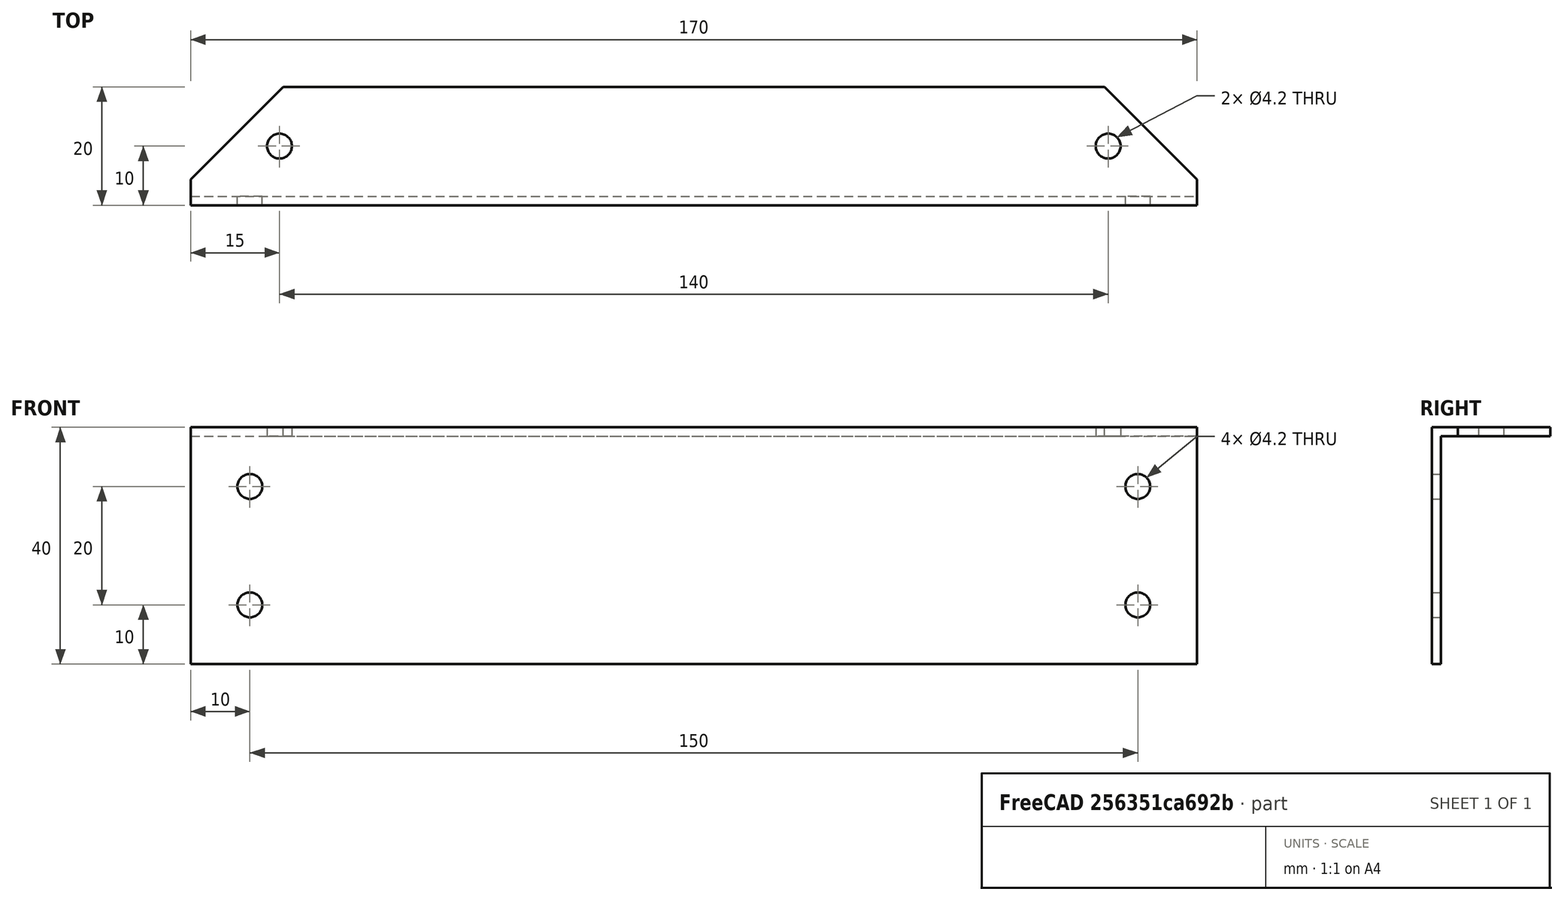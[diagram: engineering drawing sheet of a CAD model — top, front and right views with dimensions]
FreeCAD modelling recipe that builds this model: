
FCSTD DOCUMENT  (FreeCAD 1.0R39319 (Git))
Label: OCT-UBRAC-AA
License: All rights reserved
LicenseURL: https://en.wikipedia.org/wiki/All_rights_reserved
objects: TechDraw::DrawViewDimension×16, Sketcher::SketchObject×4, TechDraw::DrawProjGroupItem×3, PartDesign::Hole×2, PartDesign::Pad×1, PartDesign::Pocket×1, App::VarSet×1, PartDesign::Mirrored×1, PartDesign::Body×1, TechDraw::DrawSVGTemplate×1, TechDraw::DrawProjGroup×1, TechDraw::DrawPage×1
note: 50 computed .brp shape members not serialized (recipe doc carries the construction recipe); baked Part::Feature solids carry a one-line shape summary decoded from their .brp

FEATURE [Sketcher::SketchObject] Sketch
  ArcFitTolerance = 1e-06
  AttachmentSupport = -> [YZ_Plane]
  FullyConstrained = true
  MakeInternals = false
  MapMode = 5
  Placement = pos=(0,0,0) rot=(0.57735,0.57735,0.57735;2.0944rad)
  sketch-geometry (6):
    g0: LineSegment StartX=0 StartY=-40 StartZ=0 EndX=0 EndY=0 EndZ=0
    g1: LineSegment StartX=0 StartY=0 StartZ=0 EndX=20 EndY=0 EndZ=0
    g2: LineSegment StartX=20 StartY=0 StartZ=0 EndX=20 EndY=-1.5 EndZ=0
    g3: LineSegment StartX=20 StartY=-1.5 StartZ=0 EndX=1.5 EndY=-1.5 EndZ=0
    g4: LineSegment StartX=1.5 StartY=-1.5 StartZ=0 EndX=1.5 EndY=-40 EndZ=0
    g5: LineSegment StartX=1.5 StartY=-40 StartZ=0 EndX=0 EndY=-40 EndZ=0
  constraints (17):
    c: Coincident(g0,g1)
    c: Horizontal(g1)
    c: Coincident(g1,g2)
    c: Coincident(g2,g3)
    c: Coincident(g3,g4)
    c: Coincident(g4,g5)
    c: Coincident(g5,g0)
    c: Coincident(g0,g-1)
    c: Vertical(g2)
    c: Horizontal(g5)
    c: Vertical(g0)
    c: Vertical(g4)
    c: Horizontal(g3)
    c: DistanceX(g5,g5) = 1.5
    c: DistanceY(g0,g0) = 40
    c: DistanceY(g2,g2) = 1.5
    c: DistanceX(g1,g1) = 20
FEATURE [PartDesign::Pad] Pad
  Direction = (1,0,0)
  Length = 170
  Length2 = 10
  Midplane = true
  Placement = pos=(0,0,0) rot=(1,1,1;2.0944rad)
  Profile = -> Sketch
  ReferenceAxis = -> Sketch [N_Axis]
  Refine = true
  Suppressed = false
  Type = 0
FEATURE [Sketcher::SketchObject] Sketch002
  ArcFitTolerance = 1e-06
  AttachmentSupport = -> [XZ_Plane]
  FullyConstrained = true
  MakeInternals = false
  MapMode = 5
  Placement = pos=(0,0,0) rot=(1,0,0;1.5708rad)
  sketch-geometry (5):
    g0: Circle CenterX=-75 CenterY=-30 CenterZ=0 NormalX=0 NormalY=0 NormalZ=1 AngleXU=0 Radius=2.5
    g1: Circle CenterX=75 CenterY=-30 CenterZ=0 NormalX=0 NormalY=0 NormalZ=1 AngleXU=0 Radius=2.5
    g2: Circle CenterX=-75 CenterY=-10 CenterZ=0 NormalX=0 NormalY=0 NormalZ=1 AngleXU=0 Radius=2.5
    g3: Circle CenterX=75 CenterY=-10 CenterZ=0 NormalX=0 NormalY=0 NormalZ=1 AngleXU=0 Radius=2.5
    g4: LineSegment [constr] StartX=-75 StartY=-30 StartZ=0 EndX=-75 EndY=-10 EndZ=0
  constraints (12):
    c: Symmetric(g0,g1,g-2)
    c: DistanceX(g0,g1) = 150
    c: Diameter(g0) = 5
    c: Equal(g1,g0)
    c: Symmetric(g3,g2,g-2)
    c: Coincident(g4,g0)
    c: Coincident(g4,g2)
    c: Vertical(g4)
    c: Equal(g2,g0)
    c: Equal(g0,g3)
    c: DistanceY(g4,g4) = 20
    c: DistanceY(g2,g-1) = 10
FEATURE [PartDesign::Hole] Hole  label="panel holes"
  BaseFeature = -> Pad
  CustomThreadClearance = 0
  Depth = 355.084
  DepthType = 1
  Diameter = 4.2
  DrillForDepth = false
  DrillPoint = 1
  DrillPointAngle = 118
  HoleCutCountersinkAngle = 90
  HoleCutCustomValues = false
  HoleCutDepth = 0
  HoleCutDiameter = 6.1
  HoleCutType = 0
  ModelThread = false
  Placement = pos=(0,0,0) rot=(1,1,1;2.0944rad)
  Profile = -> Sketch002
  Refine = true
  Suppressed = false
  Tapered = false
  TaperedAngle = 90
  ThreadClass = 0
  ThreadDepth = 355.084
  ThreadDepthType = 0
  ThreadDirection = 0
  ThreadFit = 0
  ThreadSize = 0
  ThreadType = 0
  Threaded = false
  UseCustomThreadClearance = false
FEATURE [Sketcher::SketchObject] Sketch003
  ArcFitTolerance = 1e-06
  AttachmentSupport = -> [XY_Plane]
  FullyConstrained = true
  MakeInternals = false
  MapMode = 5
  sketch-geometry (2):
    g0: Circle CenterX=-70 CenterY=10 CenterZ=0 NormalX=0 NormalY=0 NormalZ=1 AngleXU=0 Radius=2.5
    g1: Circle CenterX=70 CenterY=10 CenterZ=0 NormalX=0 NormalY=0 NormalZ=1 AngleXU=0 Radius=2.5
  constraints (5):
    c: Symmetric(g1,g0,g-2)
    c: DistanceX(g0,g1) = 140
    c: Equal(g0,g1)
    c: Diameter(g1) = 5
    c: Distance(g1,g-1) = 10
FEATURE [PartDesign::Hole] Hole001  label="base holes"
  BaseFeature = -> Hole
  CustomThreadClearance = 0
  Depth = 355.084
  DepthType = 1
  Diameter = 4.2
  DrillForDepth = false
  DrillPoint = 1
  DrillPointAngle = 118
  HoleCutCountersinkAngle = 90
  HoleCutCustomValues = false
  HoleCutDepth = 0
  HoleCutDiameter = 6.1
  HoleCutType = 0
  ModelThread = false
  Placement = pos=(0,0,0) rot=(1,1,1;2.0944rad)
  Profile = -> Sketch003
  Refine = true
  Suppressed = false
  Tapered = false
  TaperedAngle = 90
  ThreadClass = 0
  ThreadDepth = 355.084
  ThreadDepthType = 0
  ThreadDirection = 0
  ThreadFit = 0
  ThreadSize = 0
  ThreadType = 0
  Threaded = false
  UseCustomThreadClearance = false
FEATURE [Sketcher::SketchObject] Sketch004
  ArcFitTolerance = 1e-06
  AttachmentSupport = -> [XY_Plane]
  FullyConstrained = false
  MakeInternals = false
  MapMode = 5
  expr: Constraints[25] = <<dims>>.octWidth
  expr: Constraints[46] = <<dims>>.width / 2
  sketch-geometry (18):
    g0: LineSegment [constr] StartX=211 StartY=298.399 StartZ=0 EndX=87.3991 EndY=422 EndZ=0
    g1: LineSegment [constr] StartX=87.3991 StartY=422 StartZ=0 EndX=-87.3991 EndY=422 EndZ=0
    g2: LineSegment [constr] StartX=-87.3991 StartY=422 StartZ=0 EndX=-211 EndY=298.399 EndZ=0
    g3: LineSegment [constr] StartX=-211 StartY=298.399 StartZ=0 EndX=-211 EndY=123.601 EndZ=0
    g4: LineSegment [constr] StartX=-211 StartY=123.601 StartZ=0 EndX=-87.3991 EndY=0 EndZ=0
    g5: LineSegment [constr] StartX=-87.3991 StartY=0 StartZ=0 EndX=87.3991 EndY=0 EndZ=0
    g6: LineSegment [constr] StartX=87.3991 StartY=0 StartZ=0 EndX=211 EndY=123.601 EndZ=0
    g7: LineSegment [constr] StartX=211 StartY=123.601 StartZ=0 EndX=211 EndY=298.399 EndZ=0
    g8: Circle [constr] CenterX=0 CenterY=211 CenterZ=0 NormalX=0 NormalY=0 NormalZ=1 AngleXU=0 Radius=228.385
    g9: LineSegment [constr] StartX=-85 StartY=0 StartZ=0 EndX=-85 EndY=4.37763 EndZ=0
    g10: LineSegment StartX=-85 StartY=4.37763 StartZ=0 EndX=-85 EndY=50 EndZ=0
    g11: LineSegment StartX=-85 StartY=50 StartZ=0 EndX=-39.3776 EndY=50 EndZ=0
    g12: LineSegment StartX=-39.3776 StartY=50 StartZ=0 EndX=-85 EndY=4.37763 EndZ=0
    g13: LineSegment [constr] StartX=-89.0955 StartY=1.69639 StartZ=0 EndX=-76.7258 EndY=14.0661 EndZ=0
    g14: LineSegment [constr] StartX=-209.304 StartY=121.905 StartZ=0 EndX=-196.934 EndY=134.274 EndZ=0
    g15: LineSegment [constr] StartX=-196.934 StartY=134.274 StartZ=0 EndX=-76.7258 EndY=14.0661 EndZ=0
    g16: LineSegment [constr] StartX=-149.2 StartY=61.8005 StartZ=0 EndX=0 EndY=211 EndZ=0
    g17: LineSegment [constr] StartX=-85 StartY=4.37763 StartZ=0 EndX=-85.7071 EndY=5.08474 EndZ=0
  constraints (46):
    c: Coincident(g0,g1)
    c: Coincident(g1,g2)
    c: Coincident(g2,g3)
    c: Coincident(g3,g4)
    c: Coincident(g4,g5)
    c: Coincident(g5,g6)
    c: Coincident(g6,g7)
    c: Coincident(g7,g0)
    c: Equal(g0, g1-g7) x7
    c: PointOnObject(g0,g8)
    c: PointOnObject(g1,g8)
    c: PointOnObject(g2,g8)
    c: PointOnObject(g3,g8)
    c: PointOnObject(g4,g8)
    c: PointOnObject(g5,g8)
    c: PointOnObject(g6,g8)
    c: PointOnObject(g7,g8)
    c: PointOnObject(g8,g-2)
    c: Horizontal(g5)
    c: DistanceY(g5,g0) = 422
    c: PointOnObject(g5,g-1)
    c: PointOnObject(g9,g5)
    c: Vertical(g9)
    c: Coincident(g9,g10)
    c: Coincident(g10,g11)
    c: Horizontal(g11)
    c: Coincident(g11,g12)
    c: Coincident(g12,g10)
    c: Vertical(g10)
    c: Angle(g11,g12) = 0.785398
    c: PointOnObject(g13,g4)
    c: Coincident(g15,g14)
    c: Coincident(g15,g13)
    c: Perpendicular(g15,g13)
    c: Perpendicular(g15,g14)
    c: Perpendicular(g4,g14)
    c: Symmetric(g4,g4,g16)
    c: Coincident(g16,g8)
    c: Symmetric(g13,g14,g16)
    c: Distance(g15,g15) = 170
    c: DistanceX(g9,g-1) = 85
    c: Coincident(g17,g9)
    c: PointOnObject(g17,g13)
    c: Perpendicular(g13,g17)
    c: Distance(g17,g17) = 1
    c: DistanceY(g-1,g10) = 50
FEATURE [PartDesign::Pocket] Pocket
  BaseFeature = -> Hole001
  Direction = (0,0,-1)
  Length = 5
  Length2 = 5
  Placement = pos=(0,0,0) rot=(1,1,1;2.0944rad)
  Profile = -> Sketch004
  ReferenceAxis = -> Sketch004 [N_Axis]
  Refine = true
  Suppressed = false
  Type = 1
FEATURE [App::VarSet] VarSet  label="dims"
  octWidth = 422
  width = 170
FEATURE [PartDesign::Mirrored] Mirrored
  BaseFeature = -> Pocket
  MirrorPlane = -> YZ_Plane
  Originals = -> [Pocket]
  Placement = pos=(0,0,0) rot=(1,1,1;2.0944rad)
  Suppressed = false
  TransformMode = 0
FEATURE [PartDesign::Body] Body  label="OCT-UBRAC-AA"
  AllowCompound = false
  Group = -> [Sketch,Pad,Sketch002,Hole,Sketch003,Hole001,Sketch004,Pocket,Mirrored]
  Origin = -> Origin
  Tip = -> Mirrored
FEATURE [TechDraw::DrawSVGTemplate] Template
  EditableTexts = approval_person=S. Aphelion; creator=M. Stoll; date_of_issue=07/02/2026; document_status=Released; document_type=Component Drawing; drawing_number=DN; general_tolerances=+- 0.1 mm; language_code=EN; part_material=Aluminium; responsible_department=RD; revision_index=A; scale=1 : 1; sheet_number=1 / 1; supplementary_title_1=Frame Upper Bracket; title=OCT-UBRAC-AA
  Height = 297
  Orientation = 1
  Template = C:/Program Files/FreeCAD 1.0/data/Mod/TechDraw/Templates/A3_Landscape_ISO5457_advanced.svg
  Width = 420
FEATURE [TechDraw::DrawProjGroupItem] View  label="Front"
  CoarseView = false
  Direction = (0,-1,0)
  Focus = 100
  HardHidden = false
  IsoCount = 0
  IsoHidden = false
  IsoVisible = false
  LockPosition = true
  Perspective = false
  Rotation = 0
  RotationVector = (1,0,0)
  ScaleType = 2
  ScrubCount = 1
  SeamHidden = false
  SeamVisible = false
  SmoothHidden = false
  SmoothVisible = true
  Source = -> [Body]
  Type = 0
  X = 0
  XDirection = (1,0,0)
  Y = 0
FEATURE [TechDraw::DrawProjGroupItem] ProjItem  label="Right"
  CoarseView = false
  Direction = (1,-1e-16,0)
  Focus = 100
  HardHidden = false
  IsoCount = 0
  IsoHidden = false
  IsoVisible = false
  LockPosition = false
  Perspective = false
  Rotation = 0
  RotationVector = (1,0,0)
  ScaleType = 0
  ScrubCount = 1
  SeamHidden = false
  SeamVisible = false
  SmoothHidden = false
  SmoothVisible = true
  Source = -> [Body]
  Type = 2
  X = 145
  XDirection = (1e-16,1,0)
  Y = 0
FEATURE [TechDraw::DrawProjGroupItem] ProjItem001  label="Top"
  CoarseView = false
  Direction = (0,0,1)
  Focus = 100
  HardHidden = false
  IsoCount = 0
  IsoHidden = false
  IsoVisible = false
  LockPosition = false
  Perspective = false
  Rotation = 0
  RotationVector = (1,0,0)
  ScaleType = 0
  ScrubCount = 1
  SeamHidden = false
  SeamVisible = false
  SmoothHidden = false
  SmoothVisible = true
  Source = -> [Body]
  Type = 4
  X = 0
  XDirection = (1,0,0)
  Y = 90
FEATURE [TechDraw::DrawProjGroup] ProjGroup
  Anchor = -> View
  AutoDistribute = true
  LockPosition = false
  ProjectionType = 1
  Rotation = 0
  ScaleType = 0
  Source = -> [Body]
  Views = -> [View,ProjItem,ProjItem001]
  X = 177.538
  Y = 142.093
  spacingX = 50
  spacingY = 60
FEATURE [TechDraw::DrawViewDimension] Dimension
  AngleOverride = false
  Arbitrary = false
  ArbitraryTolerances = false
  BoxCorners = (2) [(-10,-20,0),(10,20,0)]
  EqualTolerance = true
  ExtensionAngle = 0
  FormatSpec = %.1f
  FormatSpecOverTolerance = %+.1f
  FormatSpecUnderTolerance = %+.1f
  Inverted = false
  LineAngle = 0
  LockPosition = false
  MeasureType = 1
  OverTolerance = 0
  References2D = -> [ProjItem]
  Rotation = 0
  ScaleType = 0
  TheoreticalExact = false
  Type = 2
  UnderTolerance = 0
  X = -28.3446
  Y = 0
FEATURE [TechDraw::DrawViewDimension] Dimension001
  AngleOverride = false
  Arbitrary = false
  ArbitraryTolerances = false
  BoxCorners = (2) [(-10,-20,0),(10,20,0)]
  EqualTolerance = true
  ExtensionAngle = 0
  FormatSpec = %.1f
  FormatSpecOverTolerance = %+.1f
  FormatSpecUnderTolerance = %+.1f
  Inverted = false
  LineAngle = 0
  LockPosition = false
  MeasureType = 1
  OverTolerance = 0
  References2D = -> [ProjItem]
  Rotation = 0
  ScaleType = 0
  TheoreticalExact = false
  Type = 1
  UnderTolerance = 0
  X = 0
  Y = 39.1293
FEATURE [TechDraw::DrawViewDimension] Dimension002
  AngleOverride = false
  Arbitrary = false
  ArbitraryTolerances = false
  BoxCorners = (2) [(-10,-20,0),(10,20,0)]
  EqualTolerance = true
  ExtensionAngle = 0
  FormatSpec = %.1f
  FormatSpecOverTolerance = %+.1f
  FormatSpecUnderTolerance = %+.1f
  Inverted = false
  LineAngle = 0
  LockPosition = false
  MeasureType = 1
  OverTolerance = 0
  References2D = -> [ProjItem]
  Rotation = 0
  ScaleType = 0
  TheoreticalExact = false
  Type = 0
  UnderTolerance = 0
  X = 25.5405
  Y = 19.25
FEATURE [TechDraw::DrawViewDimension] Dimension003
  AngleOverride = false
  Arbitrary = false
  ArbitraryTolerances = false
  BoxCorners = (2) [(-10,-20,0),(10,20,0)]
  EqualTolerance = true
  ExtensionAngle = 0
  FormatSpec = %.1f
  FormatSpecOverTolerance = %+.1f
  FormatSpecUnderTolerance = %+.1f
  Inverted = false
  LineAngle = 0
  LockPosition = false
  MeasureType = 1
  OverTolerance = 0
  References2D = -> [ProjItem]
  Rotation = 0
  ScaleType = 0
  TheoreticalExact = false
  Type = 1
  UnderTolerance = 0
  X = -4.93521
  Y = -35.7666
FEATURE [TechDraw::DrawViewDimension] Dimension004
  AngleOverride = false
  Arbitrary = false
  ArbitraryTolerances = false
  BoxCorners = (2) [(-85,-20,0),(85,20,0)]
  EqualTolerance = true
  ExtensionAngle = 0
  FormatSpec = %.1f
  FormatSpecOverTolerance = %+.1f
  FormatSpecUnderTolerance = %+.1f
  Inverted = false
  LineAngle = 0
  LockPosition = false
  MeasureType = 1
  OverTolerance = 0
  References2D = -> [View]
  Rotation = 0
  ScaleType = 0
  TheoreticalExact = false
  Type = 1
  UnderTolerance = 0
  X = 0
  Y = -35.6517
FEATURE [TechDraw::DrawViewDimension] Dimension005
  AngleOverride = false
  Arbitrary = false
  ArbitraryTolerances = false
  BoxCorners = (2) [(-85,-20,0),(85,20,0)]
  EqualTolerance = true
  ExtensionAngle = 0
  FormatSpec = %.1f
  FormatSpecOverTolerance = %+.1f
  FormatSpecUnderTolerance = %+.1f
  Inverted = false
  LineAngle = 0
  LockPosition = false
  MeasureType = 1
  OverTolerance = 0
  References2D = -> [View]
  Rotation = 0
  ScaleType = 0
  TheoreticalExact = false
  Type = 0
  UnderTolerance = 0
  X = -80
  Y = 39.6021
FEATURE [TechDraw::DrawViewDimension] Dimension006
  AngleOverride = false
  Arbitrary = false
  ArbitraryTolerances = false
  BoxCorners = (2) [(-85,-20,0),(85,20,0)]
  EqualTolerance = true
  ExtensionAngle = 0
  FormatSpec = %.1f
  FormatSpecOverTolerance = %+.1f
  FormatSpecUnderTolerance = %+.1f
  Inverted = false
  LineAngle = 0
  LockPosition = false
  MeasureType = 1
  OverTolerance = 0
  References2D = -> [View]
  Rotation = 0
  ScaleType = 0
  TheoreticalExact = false
  Type = 1
  UnderTolerance = 0
  X = 4.22805
  Y = 39.6021
FEATURE [TechDraw::DrawViewDimension] Dimension007
  AngleOverride = false
  Arbitrary = false
  ArbitraryTolerances = false
  BoxCorners = (2) [(-85,-10,0),(85,10,0)]
  EqualTolerance = true
  ExtensionAngle = 0
  FormatSpec = %.1f
  FormatSpecOverTolerance = %+.1f
  FormatSpecUnderTolerance = %+.1f
  Inverted = false
  LineAngle = 0
  LockPosition = false
  MeasureType = 1
  OverTolerance = 0
  References2D = -> [ProjItem001]
  Rotation = 0
  ScaleType = 0
  TheoreticalExact = false
  Type = 0
  UnderTolerance = 0
  X = -77.5
  Y = -24.1028
FEATURE [TechDraw::DrawViewDimension] Dimension008
  AngleOverride = false
  Arbitrary = false
  ArbitraryTolerances = false
  BoxCorners = (2) [(-85,-10,0),(85,10,0)]
  EqualTolerance = true
  ExtensionAngle = 0
  FormatSpec = %.1f
  FormatSpecOverTolerance = %+.1f
  FormatSpecUnderTolerance = %+.1f
  Inverted = false
  LineAngle = 0
  LockPosition = false
  MeasureType = 1
  OverTolerance = 0
  References2D = -> [ProjItem001]
  Rotation = 0
  ScaleType = 0
  TheoreticalExact = false
  Type = 1
  UnderTolerance = 0
  X = 0
  Y = -24.1028
FEATURE [TechDraw::DrawViewDimension] Dimension009
  AngleOverride = false
  Arbitrary = false
  ArbitraryTolerances = false
  BoxCorners = (2) [(-85,-20,0),(85,20,0)]
  EqualTolerance = true
  ExtensionAngle = 0
  FormatSpec = ⌀%.1f
  FormatSpecOverTolerance = %+.1f
  FormatSpecUnderTolerance = %+.1f
  Inverted = false
  LineAngle = 0
  LockPosition = false
  MeasureType = 1
  OverTolerance = 0
  References2D = -> [View]
  Rotation = 0
  ScaleType = 0
  TheoreticalExact = false
  Type = 5
  UnderTolerance = 0
  X = -105.993
  Y = 33.5344
FEATURE [TechDraw::DrawViewDimension] Dimension010
  AngleOverride = false
  Arbitrary = false
  ArbitraryTolerances = false
  BoxCorners = (2) [(-85,-10,0),(85,10,0)]
  EqualTolerance = true
  ExtensionAngle = 0
  FormatSpec = ⌀%.1f
  FormatSpecOverTolerance = %+.1f
  FormatSpecUnderTolerance = %+.1f
  Inverted = false
  LineAngle = 0
  LockPosition = false
  MeasureType = 1
  OverTolerance = 0
  References2D = -> [ProjItem001]
  Rotation = 0
  ScaleType = 0
  TheoreticalExact = false
  Type = 5
  UnderTolerance = 0
  X = -95.1991
  Y = 26.8648
FEATURE [TechDraw::DrawViewDimension] Dimension011
  AngleOverride = false
  Arbitrary = false
  ArbitraryTolerances = false
  BoxCorners = (2) [(-85,-10,0),(85,10,0)]
  EqualTolerance = true
  ExtensionAngle = 0
  FormatSpec = %.1f
  FormatSpecOverTolerance = %+.1f
  FormatSpecUnderTolerance = %+.1f
  Inverted = false
  LineAngle = 0
  LockPosition = false
  MeasureType = 1
  OverTolerance = 0
  References2D = -> [ProjItem001]
  Rotation = 0
  ScaleType = 0
  TheoreticalExact = false
  Type = 2
  UnderTolerance = 0
  X = 102.894
  Y = 5
FEATURE [TechDraw::DrawViewDimension] Dimension012
  AngleOverride = false
  Arbitrary = false
  ArbitraryTolerances = false
  BoxCorners = (2) [(-85,-20,0),(85,20,0)]
  EqualTolerance = true
  ExtensionAngle = 0
  FormatSpec = %.1f
  FormatSpecOverTolerance = %+.1f
  FormatSpecUnderTolerance = %+.1f
  Inverted = false
  LineAngle = 0
  LockPosition = false
  MeasureType = 1
  OverTolerance = 0
  References2D = -> [View]
  Rotation = 0
  ScaleType = 0
  TheoreticalExact = false
  Type = 0
  UnderTolerance = 0
  X = 94.455
  Y = 15
FEATURE [TechDraw::DrawViewDimension] Dimension013
  AngleOverride = false
  Arbitrary = false
  ArbitraryTolerances = false
  BoxCorners = (2) [(-85,-20,0),(85,20,0)]
  EqualTolerance = true
  ExtensionAngle = 0
  FormatSpec = %.1f
  FormatSpecOverTolerance = %+.1f
  FormatSpecUnderTolerance = %+.1f
  Inverted = false
  LineAngle = 0
  LockPosition = false
  MeasureType = 1
  OverTolerance = 0
  References2D = -> [View]
  Rotation = 0
  ScaleType = 0
  TheoreticalExact = false
  Type = 2
  UnderTolerance = 0
  X = 94.455
  Y = 0
FEATURE [TechDraw::DrawViewDimension] Dimension014
  AngleOverride = false
  Arbitrary = false
  ArbitraryTolerances = false
  BoxCorners = (2) [(-85,-10,0),(85,10,0)]
  EqualTolerance = true
  ExtensionAngle = 0
  FormatSpec = %.1f
  FormatSpecOverTolerance = %+.1f
  FormatSpecUnderTolerance = %+.1f
  Inverted = false
  LineAngle = 0
  LockPosition = false
  MeasureType = 1
  OverTolerance = 0
  References2D = -> [ProjItem001]
  Rotation = 0
  ScaleType = 0
  TheoreticalExact = false
  Type = 0
  UnderTolerance = 0
  X = -107.898
  Y = -7.81118
FEATURE [TechDraw::DrawViewDimension] Dimension015
  AngleOverride = false
  Arbitrary = false
  ArbitraryTolerances = false
  BoxCorners = (2) [(-85,-10,0),(85,10,0)]
  EqualTolerance = true
  ExtensionAngle = 0
  FormatSpec = %.1f
  FormatSpecOverTolerance = %+.1f
  FormatSpecUnderTolerance = %+.1f
  Inverted = false
  LineAngle = 0
  LockPosition = false
  MeasureType = 1
  OverTolerance = 0
  References2D = -> [ProjItem001]
  Rotation = 0
  ScaleType = 0
  TheoreticalExact = false
  Type = 6
  UnderTolerance = 0
  X = 83.2101
  Y = 24.65
FEATURE [TechDraw::DrawPage] Page
  KeepUpdated = true
  NextBalloonIndex = 1
  ProjectionType = 1
  Template = -> Template
  Views = -> [ProjGroup,Dimension,Dimension001,Dimension002,Dimension003,Dimension004,Dimension005,Dimension006,Dimension007,Dimension008,Dimension009,Dimension010,Dimension011,Dimension012,Dimension013,Dimension014,Dimension015]
